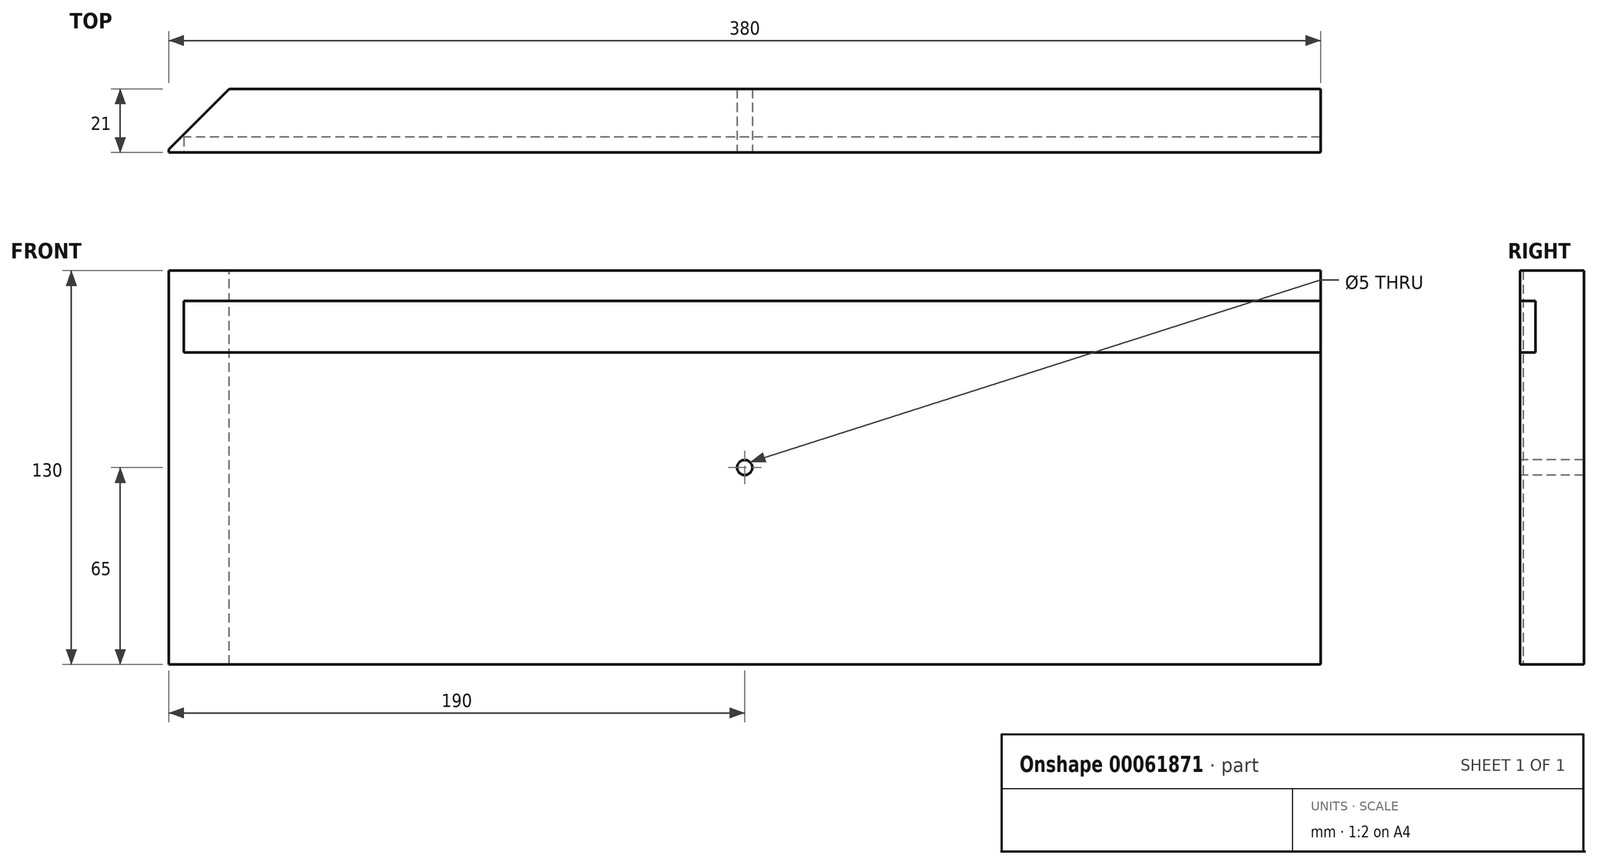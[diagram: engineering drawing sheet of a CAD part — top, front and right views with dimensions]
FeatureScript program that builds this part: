
annotation { "Feature Type Name" : "Feature", "Feature Type Description" : "" }
export const myFeature = defineFeature(function(context is Context, id is Id, definition is map)
    precondition{}
    {
        {
            var Q0;
            Q0=qCreatedBy(makeId("Front.planeOp"),FACE);
            var sketch = newSketch(context, id + "F0", { "sketchPlane" : qUnion([Q0])});
            skLineSegment(sketch, "E0.bottom", {"start": v(0, 0) * mm, "end": v(380, 0) * mm});
            skLineSegment(sketch, "E0.top", {"start": v(0, 130) * mm, "end": v(380, 130) * mm});
            skLineSegment(sketch, "E0.left", {"start": v(0, 0) * mm, "end": v(0, 130) * mm});
            skLineSegment(sketch, "E0.right", {"start": v(380, 0) * mm, "end": v(380, 130) * mm});
            skSolve(sketch);
        }
        {
            var Q0;
            Q0=makeQuery(id+"F0.imprint","IMPRINT",FACE,{"disambiguationData":[TD([[makeQuery(id+"F0.imprint","IMPRINT",EDGE,{"derivedFrom":sQuery(id+"F0.wireOp",EDGE,"E0.bottom")}),1.0]])]});
            extrude(context, id + "F1", {"entities" : qUnion([Q0]), "depth" : 21 * mm});
        }
        {
            var Q0;
            Q0=makeQuery(id+"F1.opExtrude","CAP_FACE",FACE,{"disambiguationData":[OSD([sQuery(id+"F0.wireOp",EDGE,"E0.bottom"),sQuery(id+"F0.wireOp",EDGE,"E0.top"),sQuery(id+"F0.wireOp",EDGE,"E0.left"),sQuery(id+"F0.wireOp",EDGE,"E0.right")])],"isStart":false});
            var sketch = newSketch(context, id + "F2", { "sketchPlane" : qUnion([Q0])});
            skLineSegment(sketch, "E1.bottom", {"start": v(380, 120) * mm, "end": v(5, 120) * mm});
            skLineSegment(sketch, "E1.top", {"start": v(380, 103) * mm, "end": v(5, 103) * mm});
            skLineSegment(sketch, "E1.left", {"start": v(380, 120) * mm, "end": v(380, 103) * mm});
            skLineSegment(sketch, "E1.right", {"start": v(5, 120) * mm, "end": v(5, 103) * mm});
            skSolve(sketch);
        }
        {
            var Q0;
            Q0 = qSketchRegion(id + "F2", true);
            extrude(context, id + "F3", {"entities" : qUnion([Q0]), "operationType" : NewBodyOperationType.REMOVE, "endBound" : BoundingType.SYMMETRIC, "oppositeDirection" : true, "depth" : 10.2 * mm});
        }
        {
            var Q0;
            Q0=makeQuery(id+"F1.opExtrude","CAP_EDGE",EDGE,{"disambiguationData":[OSD([sQuery(id+"F0.wireOp",EDGE,"E0.left")])],"isStart":true});
            chamfer(context, id + "F4", {"entities" : qUnion([Q0]), "width" : 20 * mm, "tangentPropagation" : true});
        }
        {
            var Q0;
            Q0=makeQuery(id+"F1.opExtrude","CAP_FACE",FACE,{"disambiguationData":[OSD([sQuery(id+"F0.wireOp",EDGE,"E0.bottom"),sQuery(id+"F0.wireOp",EDGE,"E0.top"),sQuery(id+"F0.wireOp",EDGE,"E0.left"),sQuery(id+"F0.wireOp",EDGE,"E0.right")])],"isStart":false});
            var sketch = newSketch(context, id + "F5", { "sketchPlane" : qUnion([Q0])});
            skLineSegment(sketch, "E2", {"start": v(0, 65) * mm, "end": v(380, 65) * mm, "construction": true});
            skPoint(sketch, "E3", {"position": v(190, 65) * mm});
            skSolve(sketch);
        }
        {
            var Q0;
            Q0=sQuery(id+"F5.wireOp",VERTEX,"E3");
            var Q1;
            Q1=makeQuery(id+"F1.opExtrude","SWEPT_BODY",BODY,{"disambiguationData":[OSD([sQuery(id+"F0.wireOp",EDGE,"E0.bottom"),sQuery(id+"F0.wireOp",EDGE,"E0.top"),sQuery(id+"F0.wireOp",EDGE,"E0.left"),sQuery(id+"F0.wireOp",EDGE,"E0.right")])]});
            hole(context, id + "F6", {"style" : HoleStyle.SIMPLE, "holeDiameter" : 5 * mm, "endStyle" : HoleEndStyle.THROUGH, "locations" : qUnion([Q0]), "scope" : qUnion([Q1])});
        }
    });
